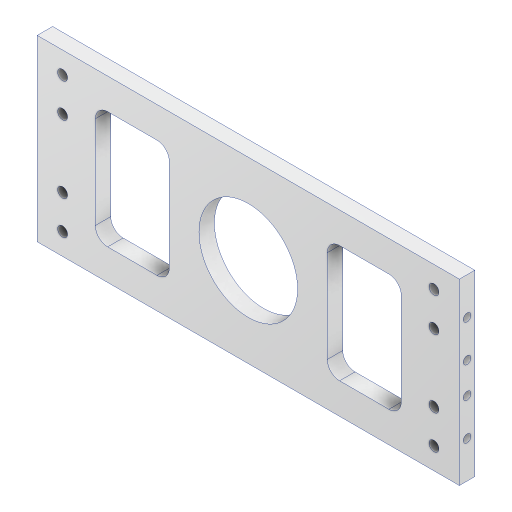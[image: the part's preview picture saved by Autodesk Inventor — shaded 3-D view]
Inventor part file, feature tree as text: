
AUTODESK INVENTOR PART (.ipt)
format: ipt  version: 2023.2 (Build 272271000, 271)  size: 446,976 bytes
history: native  units: mm
features: extrude x12, sketch x11, projected_geometry x6, other x1
ambient origin geometry x8: Origin, YZ Plane, XZ Plane, XY Plane, X Axis, Y Axis, Z Axis, Center Point
bodies: Body1 (feature_tree)
feature tree (30):
  other  "솔리드1"
  sketch  "스케치1"
  extrude  "돌출1"  Depth=58.0mm
  extrude  "돌출2"  Depth=129.5mm
  extrude  "돌출3"  Depth=3.2mm
  extrude  "돌출4"  Depth=3.2mm
  extrude  "돌출6"  Depth=3.2mm
  extrude  "돌출7"  Depth=3.2mm
  extrude  "돌출8"  Depth=7.0mm
  extrude  "돌출9"  Depth=11.0mm
  extrude  "돌출10"  Depth=7.0mm
  extrude  "돌출11"  Depth=11.0mm
  extrude  "돌출12"  Depth=4.0mm TaperAngle=0.0deg
  extrude  "돌출13"  Depth=66.0mm
  sketch  "스케치2"
  projected_geometry  "투영된 루프1"
  sketch  "스케치3"
  projected_geometry  "투영된 루프2"
  sketch  "스케치5"
  projected_geometry  "투영된 루프3"
  sketch  "스케치6"
  projected_geometry  "투영된 루프4"
  sketch  "스케치7"
  sketch  "스케치8"
  projected_geometry  "투영된 루프5"
  sketch  "스케치9"
  sketch  "스케치12"
  sketch  "스케치13"
  projected_geometry  "투영된 루프7"
  sketch  "스케치14"
